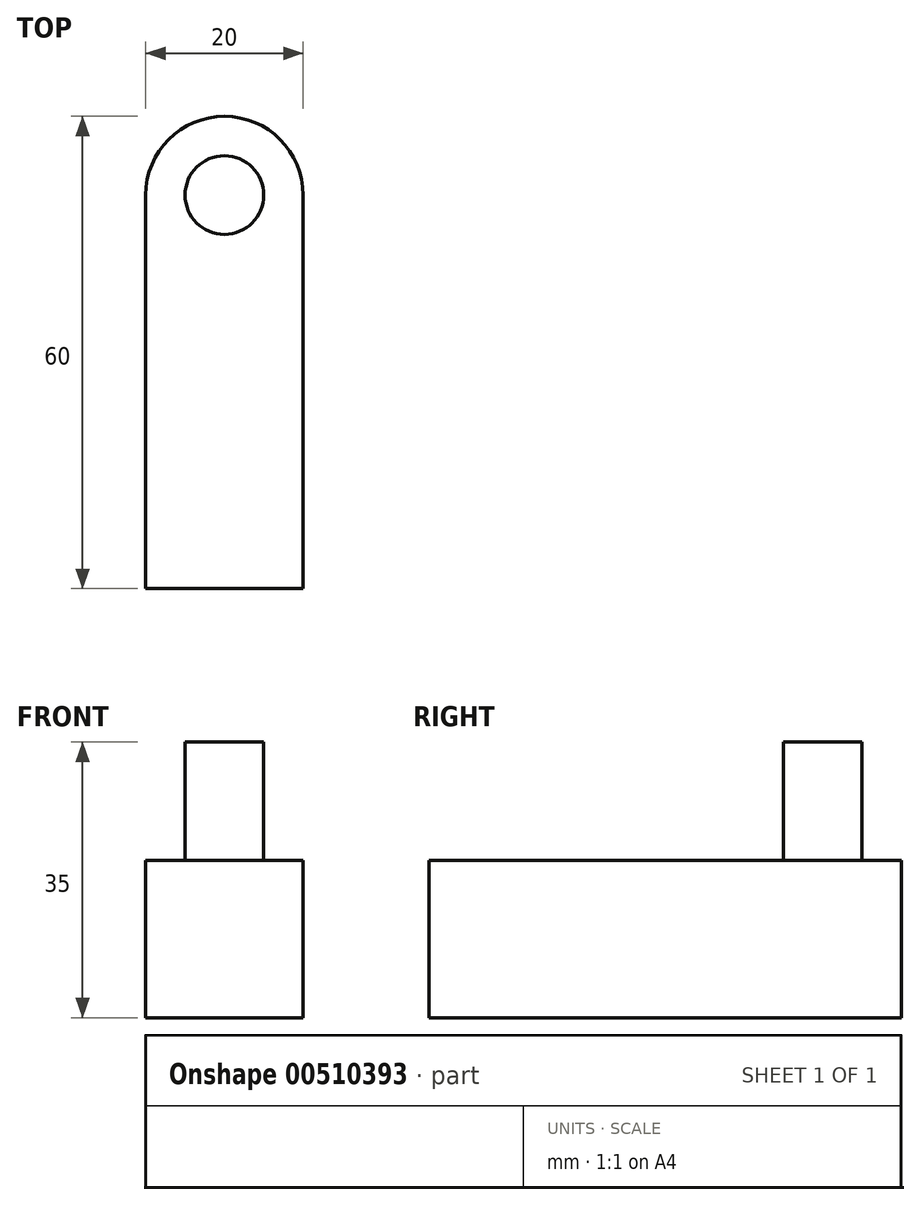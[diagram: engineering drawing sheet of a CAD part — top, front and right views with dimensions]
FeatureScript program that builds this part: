
annotation { "Feature Type Name" : "Feature", "Feature Type Description" : "" }
export const myFeature = defineFeature(function(context is Context, id is Id, definition is map)
    precondition{}
    {
        {
            var Q0;
            Q0=qCreatedBy(makeId("Top.planeOp"),FACE);
            var sketch = newSketch(context, id + "F0", { "sketchPlane" : qUnion([Q0])});
            skLineSegment(sketch, "E0.top", {"start": v(10, -25) * mm, "end": v(-10, -25) * mm});
            skLineSegment(sketch, "E0.left", {"start": v(10, 25) * mm, "end": v(10, -25) * mm});
            skLineSegment(sketch, "E0.right", {"start": v(-10, 25) * mm, "end": v(-10, -25) * mm});
            skPoint(sketch, "E0.middle", {"position": v(0, 0) * mm});
            skArc(sketch, "E1", {"start": v(10, 25) * mm, "mid": v(0, 35) * mm, "end": v(-10, 25) * mm});
            skCircle(sketch, "E2", {"center": v(0, 25) * mm, "radius": 5 * mm});
            skSolve(sketch);
        }
        {
            var Q0;
            Q0 = qSketchRegion(id + "F0", true);
            extrude(context, id + "F1", {"entities" : qUnion([Q0]), "endBound" : BoundingType.SYMMETRIC, "depth" : 20 * mm});
        }
        {
            var Q0;
            Q0=qCreatedBy(makeId("Top.planeOp"),FACE);
            var sketch = newSketch(context, id + "F2", { "sketchPlane" : qUnion([Q0])});
            skCircle(sketch, "E3", {"center": v(0, 25) * mm, "radius": 5 * mm});
            skSolve(sketch);
        }
        {
            var Q0;
            Q0=makeQuery(id+"F2.imprint","IMPRINT",FACE,{"disambiguationData":[TD([[makeQuery(id+"F2.imprint","IMPRINT",EDGE,{"derivedFrom":sQuery(id+"F2.wireOp",EDGE,"E3")}),1.0]])]});
            extrude(context, id + "F3", {"entities" : qUnion([Q0]), "operationType" : NewBodyOperationType.ADD, "endBound" : BoundingType.SYMMETRIC, "depth" : 50 * mm});
        }
        {
            var Q0;
            Q0=makeQuery(id+"F3.opExtrude","CAP_FACE",FACE,{"disambiguationData":[OSD([sQuery(id+"F2.wireOp",EDGE,"E3")])],"isStart":true});
            extrude(context, id + "F4", {"entities" : qUnion([Q0]), "operationType" : NewBodyOperationType.REMOVE, "oppositeDirection" : true, "depth" : 15 * mm});
        }
    });
